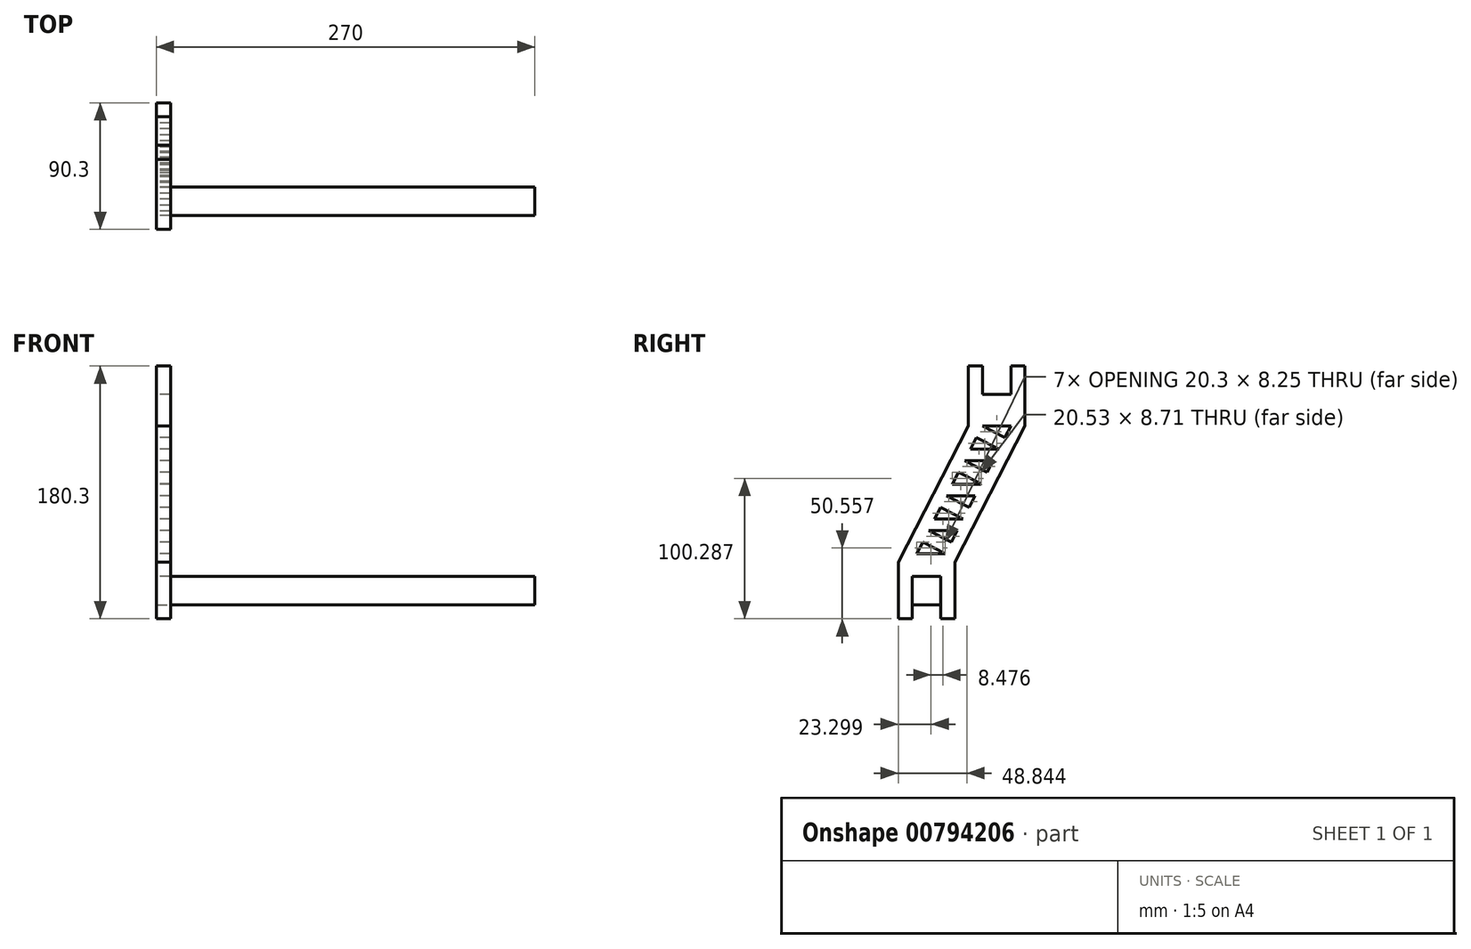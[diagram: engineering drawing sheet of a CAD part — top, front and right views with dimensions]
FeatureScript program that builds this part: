
annotation { "Feature Type Name" : "Feature", "Feature Type Description" : "" }
export const myFeature = defineFeature(function(context is Context, id is Id, definition is map)
    precondition{}
    {
        {
            var Q0;
            Q0=qCreatedBy(makeId("Front.planeOp"),FACE);
            var sketch = newSketch(context, id + "F0", { "sketchPlane" : qUnion([Q0])});
            skLineSegment(sketch, "E0.bottom", {"start": v(-135, 20.3) * mm, "end": v(135, 20.3) * mm});
            skLineSegment(sketch, "E0.top", {"start": v(-135, 0) * mm, "end": v(135, 0) * mm});
            skLineSegment(sketch, "E0.left", {"start": v(-135, 20.3) * mm, "end": v(-135, 0) * mm});
            skLineSegment(sketch, "E0.right", {"start": v(135, 20.3) * mm, "end": v(135, 0) * mm});
            skSolve(sketch);
        }
        {
            var Q0;
            Q0=makeQuery(id+"F0.imprint","IMPRINT",FACE,{"disambiguationData":[TD([[makeQuery(id+"F0.imprint","IMPRINT",EDGE,{"derivedFrom":sQuery(id+"F0.wireOp",EDGE,"E0.bottom")}),-1.0]])]});
            extrude(context, id + "F1", {"entities" : qUnion([Q0]), "depth" : 20.3 * mm, "offsetDistance" : 25 * mm});
        }
        {
            var Q0;
            Q0=makeQuery(id+"F1.opExtrude","SWEPT_FACE",FACE,{"disambiguationData":[OSD([sQuery(id+"F0.wireOp",EDGE,"E0.left")])]});
            var sketch = newSketch(context, id + "F2", { "sketchPlane" : qUnion([Q0])});
            skLineSegment(sketch, "E1", {"start": v(0, -10) * mm, "end": v(0, 20.3) * mm});
            skLineSegment(sketch, "E2", {"start": v(-60, 170.3) * mm, "end": v(-60, 127.64) * mm});
            skLineSegment(sketch, "E3", {"start": v(-60, 127.64) * mm, "end": v(-10, 30.3) * mm});
            skLineSegment(sketch, "E4", {"start": v(-10, 30.3) * mm, "end": v(-10, -10) * mm});
            skLineSegment(sketch, "E5", {"start": v(-10, -10) * mm, "end": v(0, -10) * mm});
            skLineSegment(sketch, "E6", {"start": v(20.3, -10) * mm, "end": v(20.3, 20.3) * mm});
            skLineSegment(sketch, "E7", {"start": v(20.3, -10) * mm, "end": v(30.3, -10) * mm});
            skLineSegment(sketch, "E8", {"start": v(30.3, -10) * mm, "end": v(30.3, 30.3) * mm});
            skLineSegment(sketch, "E9", {"start": v(30.3, 30.3) * mm, "end": v(-19.7, 127.64) * mm});
            skLineSegment(sketch, "E10", {"start": v(-19.7, 127.64) * mm, "end": v(-19.7, 170.3) * mm});
            skLineSegment(sketch, "E11", {"start": v(-60, 170.3) * mm, "end": v(-50, 170.3) * mm});
            skLineSegment(sketch, "E12", {"start": v(-50, 170.3) * mm, "end": v(-50, 150) * mm});
            skLineSegment(sketch, "E13", {"start": v(-50, 150) * mm, "end": v(-29.7, 150) * mm});
            skLineSegment(sketch, "E14", {"start": v(-29.7, 150) * mm, "end": v(-29.7, 170.3) * mm});
            skLineSegment(sketch, "E15", {"start": v(-29.7, 170.3) * mm, "end": v(-19.7, 170.3) * mm});
            skSolve(sketch);
        }
        {
            var Q0;
            Q0=makeQuery(id+"F2.imprint","IMPRINT",FACE,{"disambiguationData":[TD([[makeQuery(id+"F2.imprint","IMPRINT",EDGE,{"derivedFrom":sQuery(id+"F2.wireOp",EDGE,"E2")}),1.0]])]});
            extrude(context, id + "F3", {"entities" : qUnion([Q0]), "oppositeDirection" : true, "depth" : 10 * mm, "offsetDistance" : 25 * mm});
        }
        {
            var Q0;
            Q0=makeQuery(id+"F3.opExtrude","CAP_FACE",FACE,{"disambiguationData":[OSD([sQuery(id+"F0.wireOp",EDGE,"E0.bottom"),sQuery(id+"F0.wireOp",EDGE,"E0.left"),sQuery(id+"F2.wireOp",EDGE,"E1"),sQuery(id+"F2.wireOp",EDGE,"E2"),sQuery(id+"F2.wireOp",EDGE,"E3"),sQuery(id+"F2.wireOp",EDGE,"E4"),sQuery(id+"F2.wireOp",EDGE,"E5"),sQuery(id+"F2.wireOp",EDGE,"E6"),sQuery(id+"F2.wireOp",EDGE,"E7"),sQuery(id+"F2.wireOp",EDGE,"E8"),sQuery(id+"F2.wireOp",EDGE,"E9"),sQuery(id+"F2.wireOp",EDGE,"E10"),sQuery(id+"F2.wireOp",EDGE,"E11"),sQuery(id+"F2.wireOp",EDGE,"E12"),sQuery(id+"F2.wireOp",EDGE,"E13"),sQuery(id+"F2.wireOp",EDGE,"E14"),sQuery(id+"F2.wireOp",EDGE,"E15")])],"isStart":true});
            var sketch = newSketch(context, id + "F4", { "sketchPlane" : qUnion([Q0])});
            skLineSegment(sketch, "E16", {"start": v(-29.7, 127.64) * mm, "end": v(20.3, 30.3) * mm});
            skLineSegment(sketch, "E17", {"start": v(20.3, 30.3) * mm, "end": v(0, 30.3) * mm});
            skLineSegment(sketch, "E18", {"start": v(0, 30.3) * mm, "end": v(-50, 127.64) * mm});
            skLineSegment(sketch, "E19", {"start": v(-50, 127.64) * mm, "end": v(-29.7, 127.64) * mm});
            skPoint(sketch, "E20.endSnap0", {"position": v(-39.85, 127.64) * mm});
            skLineSegment(sketch, "E21", {"start": v(-29.7, 127.64) * mm, "end": v(-45.76, 119.4) * mm});
            skLineSegment(sketch, "E22", {"start": v(-45.76, 119.4) * mm, "end": v(-25.46, 119.4) * mm});
            skLineSegment(sketch, "E23", {"start": v(-25.46, 119.4) * mm, "end": v(-41.52, 111.14) * mm});
            skLineSegment(sketch, "E24", {"start": v(-41.52, 111.14) * mm, "end": v(-21.22, 111.14) * mm});
            skLineSegment(sketch, "E25", {"start": v(-21.22, 111.14) * mm, "end": v(-37.29, 102.9) * mm});
            skLineSegment(sketch, "E26", {"start": v(-37.29, 102.9) * mm, "end": v(-16.99, 102.9) * mm});
            skLineSegment(sketch, "E27", {"start": v(-16.99, 102.9) * mm, "end": v(-33.05, 94.64) * mm});
            skLineSegment(sketch, "E28", {"start": v(-33.05, 94.64) * mm, "end": v(-12.75, 94.64) * mm});
            skLineSegment(sketch, "E29", {"start": v(-12.75, 94.64) * mm, "end": v(-29.7, 85.93) * mm});
            skLineSegment(sketch, "E30", {"start": v(-29.7, 85.93) * mm, "end": v(-8.28, 85.93) * mm});
            skLineSegment(sketch, "E31", {"start": v(-8.28, 85.93) * mm, "end": v(-24.34, 77.68) * mm});
            skLineSegment(sketch, "E32", {"start": v(-24.34, 77.68) * mm, "end": v(-4.04, 77.68) * mm});
            skLineSegment(sketch, "E33", {"start": v(-4.04, 77.68) * mm, "end": v(-20.1, 69.43) * mm});
            skLineSegment(sketch, "E34", {"start": v(-20.1, 69.43) * mm, "end": v(0.2, 69.43) * mm});
            skLineSegment(sketch, "E35", {"start": v(0.2, 69.43) * mm, "end": v(-15.86, 61.18) * mm});
            skLineSegment(sketch, "E36", {"start": v(-15.86, 61.18) * mm, "end": v(4.44, 61.18) * mm});
            skLineSegment(sketch, "E37", {"start": v(4.44, 61.18) * mm, "end": v(-11.63, 52.93) * mm});
            skLineSegment(sketch, "E38", {"start": v(-11.63, 52.93) * mm, "end": v(8.67, 52.93) * mm});
            skLineSegment(sketch, "E39", {"start": v(8.67, 52.93) * mm, "end": v(-7.39, 44.68) * mm});
            skLineSegment(sketch, "E40", {"start": v(-7.39, 44.68) * mm, "end": v(12.91, 44.68) * mm});
            skLineSegment(sketch, "E41", {"start": v(12.91, 44.68) * mm, "end": v(-3.15, 36.43) * mm});
            skLineSegment(sketch, "E42", {"start": v(-3.15, 36.43) * mm, "end": v(17.15, 36.43) * mm});
            skSolve(sketch);
        }
        {
            var Q0;
            {var subQ0=sQuery(id+"F4.wireOp",EDGE,"E19");Q0=makeQuery(id+"F4.imprint","IMPRINT",FACE,{"disambiguationData":[TD([[makeQuery(id+"F4.imprint","IMPRINT",EDGE,{"derivedFrom":subQ0}),-1.0]])]});}
            var Q1;
            {var subQ0=sQuery(id+"F4.wireOp",EDGE,"E23");Q1=makeQuery(id+"F4.imprint","IMPRINT",FACE,{"disambiguationData":[TD([[makeQuery(id+"F4.imprint","IMPRINT",EDGE,{"derivedFrom":subQ0}),1.0]])]});}
            var Q2;
            {var subQ0=sQuery(id+"F4.wireOp",EDGE,"E26");Q2=makeQuery(id+"F4.imprint","IMPRINT",FACE,{"disambiguationData":[TD([[makeQuery(id+"F4.imprint","IMPRINT",EDGE,{"derivedFrom":subQ0}),-1.0]])]});}
            var Q3;
            {var subQ3=sQuery(id+"F4.wireOp",EDGE,"E30");var subQ5=sQuery(id+"F4.wireOp",EDGE,"E18");var subQ6=makeQuery(id+"F4.imprint","INTERSECT",VERTEX,{"derivedFrom":[subQ5,subQ3]});Q3=makeQuery(id+"F4.imprint","IMPRINT",FACE,{"disambiguationData":[TD([[makeQuery(id+"F4.imprint","IMPRINT",EDGE,{"disambiguationData":[TD([[subQ6,-1.0]])],"derivedFrom":subQ5}),-1.0]])]});}
            var Q4;
            {var subQ0=sQuery(id+"F4.wireOp",EDGE,"E32");Q4=makeQuery(id+"F4.imprint","IMPRINT",FACE,{"disambiguationData":[TD([[makeQuery(id+"F4.imprint","IMPRINT",EDGE,{"derivedFrom":subQ0}),-1.0]])]});}
            var Q5;
            {var subQ0=sQuery(id+"F4.wireOp",EDGE,"E35");Q5=makeQuery(id+"F4.imprint","IMPRINT",FACE,{"disambiguationData":[TD([[makeQuery(id+"F4.imprint","IMPRINT",EDGE,{"derivedFrom":subQ0}),1.0]])]});}
            var Q6;
            {var subQ0=sQuery(id+"F4.wireOp",EDGE,"E38");Q6=makeQuery(id+"F4.imprint","IMPRINT",FACE,{"disambiguationData":[TD([[makeQuery(id+"F4.imprint","IMPRINT",EDGE,{"derivedFrom":subQ0}),-1.0]])]});}
            var Q7;
            {var subQ0=sQuery(id+"F4.wireOp",EDGE,"E41");Q7=makeQuery(id+"F4.imprint","IMPRINT",FACE,{"disambiguationData":[TD([[makeQuery(id+"F4.imprint","IMPRINT",EDGE,{"derivedFrom":subQ0}),1.0]])]});}
            extrude(context, id + "F5", {"entities" : qUnion([Q0, Q1, Q2, Q3, Q4, Q5, Q6, Q7]), "operationType" : NewBodyOperationType.REMOVE, "oppositeDirection" : true, "depth" : 25 * mm, "offsetDistance" : 25 * mm});
        }
    });
